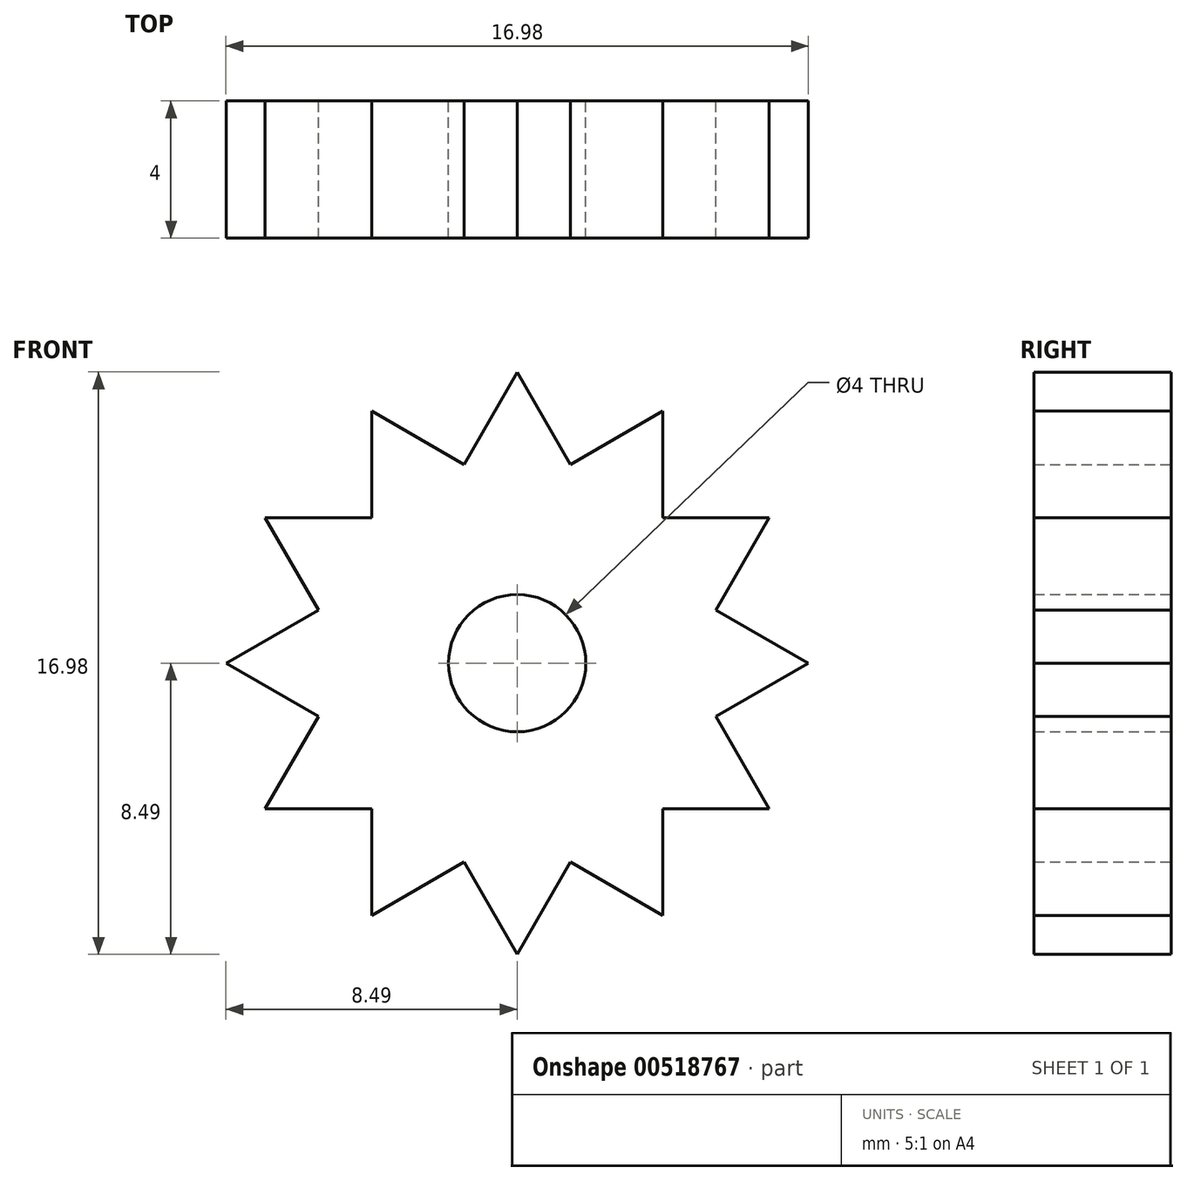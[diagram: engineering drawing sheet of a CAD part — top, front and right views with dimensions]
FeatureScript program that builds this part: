
annotation { "Feature Type Name" : "Feature", "Feature Type Description" : "" }
export const myFeature = defineFeature(function(context is Context, id is Id, definition is map)
    precondition{}
    {
        {
            var Q0;
            Q0=qCreatedBy(makeId("Front.planeOp"),FACE);
            var sketch = newSketch(context, id + "F0", { "sketchPlane" : qUnion([Q0])});
            skCircle(sketch, "E0", {"center": v(0, 0) * mm, "radius": 6 * mm});
            skCircle(sketch, "E1", {"center": v(0, 0) * mm, "radius": 2 * mm});
            skLineSegment(sketch, "E2", {"start": v(0, 0) * mm, "end": v(-1.55, 5.8) * mm, "construction": true});
            skLineSegment(sketch, "E3", {"start": v(-1.55, 5.8) * mm, "end": v(0, 8.49) * mm});
            skLineSegment(sketch, "E4", {"start": v(0, 8.49) * mm, "end": v(1.55, 5.8) * mm});
            skLineSegment(sketch, "E5.1.0", {"start": v(-4.24, 4.24) * mm, "end": v(-4.24, 7.35) * mm});
            skLineSegment(sketch, "E5.1.1", {"start": v(-4.24, 7.35) * mm, "end": v(-1.55, 5.8) * mm});
            skLineSegment(sketch, "E5.2.0", {"start": v(-5.8, 1.55) * mm, "end": v(-7.35, 4.24) * mm});
            skLineSegment(sketch, "E5.2.1", {"start": v(-7.35, 4.24) * mm, "end": v(-4.24, 4.24) * mm});
            skLineSegment(sketch, "E5.3.0", {"start": v(-5.8, -1.55) * mm, "end": v(-8.49, 0) * mm});
            skLineSegment(sketch, "E5.3.1", {"start": v(-8.49, 0) * mm, "end": v(-5.8, 1.55) * mm});
            skLineSegment(sketch, "E5.4.0", {"start": v(-4.24, -4.24) * mm, "end": v(-7.35, -4.24) * mm});
            skLineSegment(sketch, "E5.4.1", {"start": v(-7.35, -4.24) * mm, "end": v(-5.8, -1.55) * mm});
            skLineSegment(sketch, "E5.5.0", {"start": v(-1.55, -5.8) * mm, "end": v(-4.24, -7.35) * mm});
            skLineSegment(sketch, "E5.5.1", {"start": v(-4.24, -7.35) * mm, "end": v(-4.24, -4.24) * mm});
            skLineSegment(sketch, "E5.6.0", {"start": v(1.55, -5.8) * mm, "end": v(0, -8.49) * mm});
            skLineSegment(sketch, "E5.6.1", {"start": v(0, -8.49) * mm, "end": v(-1.55, -5.8) * mm});
            skLineSegment(sketch, "E5.7.0", {"start": v(4.24, -4.24) * mm, "end": v(4.24, -7.35) * mm});
            skLineSegment(sketch, "E5.7.1", {"start": v(4.24, -7.35) * mm, "end": v(1.55, -5.8) * mm});
            skLineSegment(sketch, "E5.8.0", {"start": v(5.8, -1.55) * mm, "end": v(7.35, -4.24) * mm});
            skLineSegment(sketch, "E5.8.1", {"start": v(7.35, -4.24) * mm, "end": v(4.24, -4.24) * mm});
            skLineSegment(sketch, "E5.9.0", {"start": v(5.8, 1.55) * mm, "end": v(8.49, 0) * mm});
            skLineSegment(sketch, "E5.9.1", {"start": v(8.49, 0) * mm, "end": v(5.8, -1.55) * mm});
            skLineSegment(sketch, "E5.10.0", {"start": v(4.24, 4.24) * mm, "end": v(7.35, 4.24) * mm});
            skLineSegment(sketch, "E5.10.1", {"start": v(7.35, 4.24) * mm, "end": v(5.8, 1.55) * mm});
            skLineSegment(sketch, "E5.11.0", {"start": v(1.55, 5.8) * mm, "end": v(4.24, 7.35) * mm});
            skLineSegment(sketch, "E5.11.1", {"start": v(4.24, 7.35) * mm, "end": v(4.24, 4.24) * mm});
            skSolve(sketch);
        }
        {
            var Q0;
            Q0 = qSketchRegion(id + "F0", true);
            extrude(context, id + "F1", {"entities" : qUnion([Q0]), "endBound" : BoundingType.SYMMETRIC, "depth" : 4 * mm, "offsetDistance" : 25 * mm});
        }
    });
